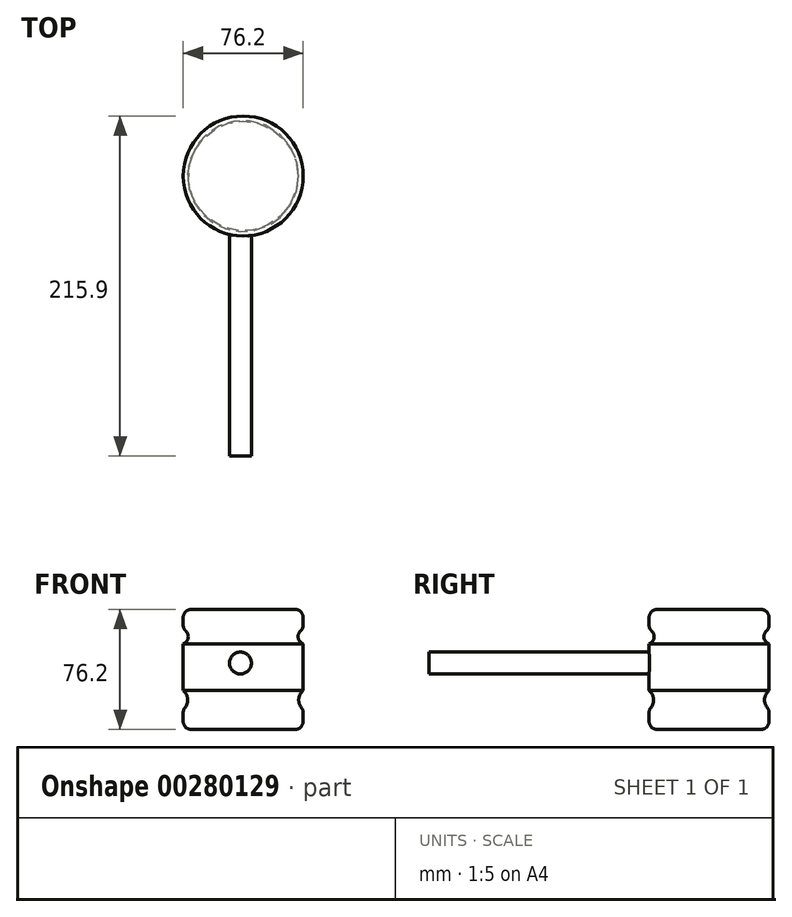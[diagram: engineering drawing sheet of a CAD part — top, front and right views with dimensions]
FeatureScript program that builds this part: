
annotation { "Feature Type Name" : "Feature", "Feature Type Description" : "" }
export const myFeature = defineFeature(function(context is Context, id is Id, definition is map)
    precondition{}
    {
        {
            var Q0;
            Q0=qCreatedBy(makeId("Front.planeOp"),FACE);
            var sketch = newSketch(context, id + "F0", { "sketchPlane" : qUnion([Q0])});
            skLineSegment(sketch, "E0", {"start": v(-39.62, 51.49) * mm, "end": v(-1.52, 51.49) * mm});
            skLineSegment(sketch, "E1", {"start": v(-1.52, 51.49) * mm, "end": v(-1.52, -24.71) * mm});
            skLineSegment(sketch, "E2", {"start": v(-1.52, -24.71) * mm, "end": v(-39.62, -24.71) * mm});
            skLineSegment(sketch, "E3", {"start": v(-39.62, -24.71) * mm, "end": v(-39.62, -12.01) * mm});
            skLineSegment(sketch, "E4", {"start": v(-39.62, 51.49) * mm, "end": v(-39.62, 38.79) * mm});
            skArc(sketch, "E5", {"start": v(-39.62, 29.64) * mm, "mid": v(-36.37, 34.21) * mm, "end": v(-39.62, 38.79) * mm});
            skLineSegment(sketch, "E6", {"start": v(-39.62, 29.64) * mm, "end": v(-39.62, 0) * mm});
            skArc(sketch, "E7", {"start": v(-39.62, -12.01) * mm, "mid": v(-36.76, -6) * mm, "end": v(-39.62, 0) * mm});
            skSolve(sketch);
        }
        {
            var Q0;
            Q0 = qSketchRegion(id + "F0", true);
            var Q1;
            Q1=sQuery(id+"F0.wireOp",EDGE,"E1");
            revolve(context, id + "F1", {"entities" : qUnion([Q0]), "axis" : qUnion([Q1]), "revolveType" : RevolveType.FULL});
        }
        {
            var Q0;
            Q0=makeQuery(id+"F1.opRevolve","SWEPT_FACE",FACE,{"disambiguationData":[OSD([sQuery(id+"F0.wireOp",EDGE,"E4")])]});
            var Q1;
            Q1=makeQuery(id+"F1.opRevolve","SWEPT_FACE",FACE,{"disambiguationData":[OSD([sQuery(id+"F0.wireOp",EDGE,"E3")])]});
            fillet(context, id + "F2", {"entities" : qUnion([Q0, Q1]), "radius" : 5.08 * mm, "tangentPropagation" : true, "allowEdgeOverflow" : false});
        }
        {
            var Q0;
            Q0=qCreatedBy(makeId("Front.planeOp"),FACE);
            var sketch = newSketch(context, id + "F3", { "sketchPlane" : qUnion([Q0])});
            skCircle(sketch, "E8", {"center": v(-3.24, 17.5) * mm, "radius": 6.99 * mm});
            skSolve(sketch);
        }
        {
            var Q0;
            Q0 = qSketchRegion(id + "F3", true);
            extrude(context, id + "F4", {"entities" : qUnion([Q0]), "operationType" : NewBodyOperationType.ADD, "depth" : 177.8 * mm});
        }
    });
